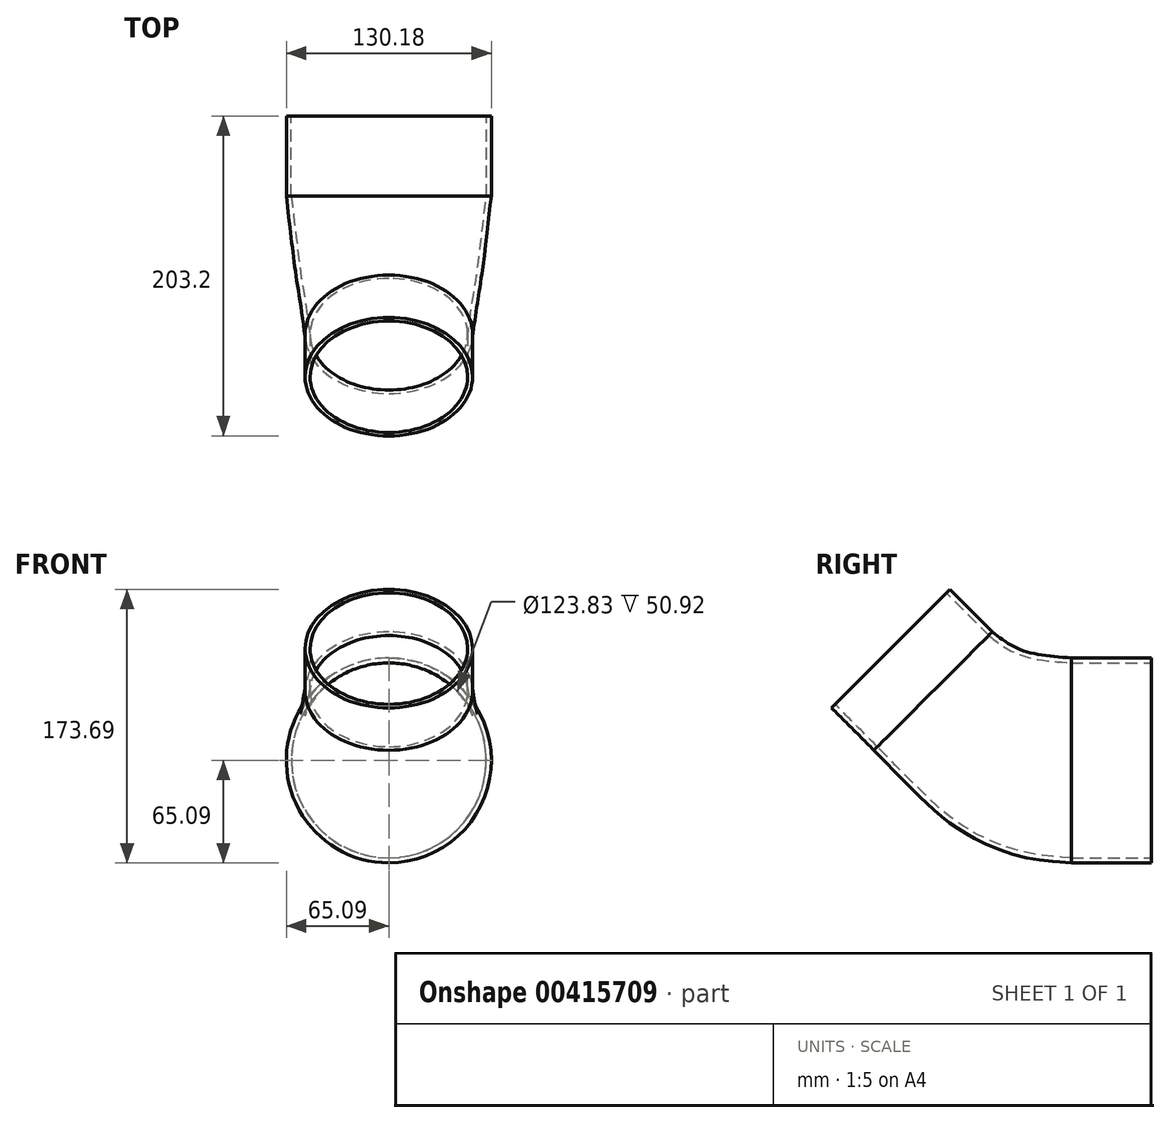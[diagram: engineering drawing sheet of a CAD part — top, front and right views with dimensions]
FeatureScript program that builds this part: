
annotation { "Feature Type Name" : "Feature", "Feature Type Description" : "" }
export const myFeature = defineFeature(function(context is Context, id is Id, definition is map)
    precondition{}
    {
        {
            var Q0;
            Q0=qCreatedBy(makeId("Front.planeOp"),FACE);
            var sketch = newSketch(context, id + "F0", { "sketchPlane" : qUnion([Q0])});
            skCircle(sketch, "E0", {"center": v(0, 0) * mm, "radius": 65.09 * mm});
            skSolve(sketch);
        }
        {
            var Q0;
            Q0=makeQuery(id+"F0.imprint","IMPRINT",FACE,{"disambiguationData":[TD([[makeQuery(id+"F0.imprint","IMPRINT",EDGE,{"derivedFrom":sQuery(id+"F0.wireOp",EDGE,"E0")}),1.0]])]});
            extrude(context, id + "F1", {"entities" : qUnion([Q0]), "depth" : 50.8 * mm});
        }
        {
            var Q0;
            Q0=qCreatedBy(makeId("Right.planeOp"),FACE);
            var sketch = newSketch(context, id + "F2", { "sketchPlane" : qUnion([Q0])});
            skLineSegment(sketch, "E1", {"start": v(0, -65.09) * mm, "end": v(-50.8, -65.09) * mm});
            skLineSegment(sketch, "E2", {"start": v(-50.8, 65.09) * mm, "end": v(0, 65.09) * mm});
            skLineSegment(sketch, "E3", {"start": v(-50.8, 65.09) * mm, "end": v(-142.85, -26.96) * mm, "construction": true});
            skLineSegment(sketch, "E4", {"start": v(0, 65.09) * mm, "end": v(-203.2, 65.09) * mm, "construction": true});
            skLineSegment(sketch, "E5", {"start": v(-142.85, -26.96) * mm, "end": v(-203.2, 33.4) * mm});
            skLineSegment(sketch, "E6", {"start": v(-203.2, 65.09) * mm, "end": v(-203.2, 33.4) * mm, "construction": true});
            skLineSegment(sketch, "E7", {"start": v(-203.2, 33.4) * mm, "end": v(-110.4, 126.2) * mm, "construction": true});
            skArc(sketch, "E8.trimOffspring", {"start": v(-142.85, -26.96) * mm, "mid": v(-100.62, -55.18) * mm, "end": v(-50.8, -65.09) * mm});
            skArc(sketch, "E9", {"start": v(-96.82, 19.06) * mm, "mid": v(-75.7, 4.95) * mm, "end": v(-50.8, 0) * mm});
            skLineSegment(sketch, "E10.0", {"start": v(-50.8, -65.09) * mm, "end": v(-50.8, 65.09) * mm});
            skSolve(sketch);
        }
        {
            var Q0;
            Q0=sQuery(id+"F2.wireOp",EDGE,"E7");
            cPlane(context, id + "F3", {"entities" : qUnion([Q0]), "cplaneType" : CPlaneType.LINE_ANGLE, "offset" : 25.4 * mm, "angle" : 0 * degree, "width" : 152.4 * mm, "height" : 152.4 * mm});
        }
        {
            var Q0;
            Q0=qCreatedBy(id+"F3.planeOp",FACE);
            var sketch = newSketch(context, id + "F4", { "sketchPlane" : qUnion([Q0])});
            skLineSegment(sketch, "E11.0", {"start": v(0, -120.07) * mm, "end": v(0, 11.18) * mm, "construction": true});
            skCircle(sketch, "E12", {"center": v(0, -66.9) * mm, "radius": 53.18 * mm});
            skSolve(sketch);
        }
        {
            var Q0;
            Q0=makeQuery(id+"F4.imprint","IMPRINT",FACE,{"disambiguationData":[TD([[makeQuery(id+"F4.imprint","IMPRINT",EDGE,{"derivedFrom":sQuery(id+"F4.wireOp",EDGE,"E12")}),1.0]])]});
            var Q1;
            Q1=sQuery(id+"F4.wireOp",EDGE,"E11.0");
            var Q2;
            Q2=sQuery(id+"F4.wireOp",EDGE,"E12");
            extrude(context, id + "F5", {"entities" : qUnion([Q0]), "operationType" : NewBodyOperationType.ADD, "surfaceEntities" : qUnion([Q1, Q2]), "oppositeDirection" : true, "depth" : 38.1 * mm});
        }
        {
            var Q0;
            Q0=qCreatedBy(makeId("Right.planeOp"),FACE);
            var sketch = newSketch(context, id + "F6", { "sketchPlane" : qUnion([Q0])});
            skPoint(sketch, "E13.0", {"position": v(-50.8, 65.09) * mm});
            skPoint(sketch, "E14.0", {"position": v(-50.8, -65.09) * mm});
            skLineSegment(sketch, "E15.0", {"start": v(-50.8, 65.09) * mm, "end": v(-142.85, -26.96) * mm, "construction": true});
            skLineSegment(sketch, "E16", {"start": v(-128, 108.6) * mm, "end": v(-101.05, 81.66) * mm, "construction": true});
            skFitSpline(sketch, "E17", {"points": [v(-50.8, 65.09) * mm, v(-82.75, 70.17) * mm, v(-101.05, 81.66) * mm], "startDerivative": vector(-62.84, 4.75) * mm, "endDerivative": vector(-36.78, 29.22) * mm});
            skLineSegment(sketch, "E18.0", {"start": v(-142.85, -26.96) * mm, "end": v(-176.26, 6.45) * mm});
            skArc(sketch, "E19.0", {"start": v(-142.85, -26.96) * mm, "mid": v(-100.62, -55.18) * mm, "end": v(-50.8, -65.09) * mm});
            skPoint(sketch, "E20.orphan", {"position": v(-203.2, 33.4) * mm});
            skFitSpline(sketch, "E21", {"points": [v(-50.8, -65.09) * mm, v(-85.52, -60.37) * mm, v(-117.86, -46.48) * mm, v(-139.58, -30.11) * mm, v(-176.26, 6.45) * mm], "startDerivative": vector(-142.28, 10.17) * mm, "endDerivative": vector(-133.17, 136.5) * mm});
            skSolve(sketch);
        }
        {
            var Q0;
            Q0=makeQuery(id+"F1.opExtrude","CAP_FACE",FACE,{"disambiguationData":[OSD([sQuery(id+"F0.wireOp",EDGE,"E0")])],"isStart":false});
            var Q1;
            Q1=makeQuery(id+"F5.opExtrude","CAP_FACE",FACE,{"disambiguationData":[OSD([sQuery(id+"F4.wireOp",EDGE,"E12")])],"isStart":false});
            var Q2;
            Q2=sQuery(id+"F6.wireOp",EDGE,"E17");
            var Q3;
            Q3=sQuery(id+"F6.wireOp",EDGE,"E21");
            loft(context, id + "F7", {"operationType" : NewBodyOperationType.ADD, "addGuides" : true, "sheetProfilesArray" : [{ "sheetProfileEntities" : qUnion([Q0]) }, { "sheetProfileEntities" : qUnion([Q1]) }], "guidesArray" : [{ "guideEntities" : qUnion([Q2]), "guideDerivativeType" : LoftGuideDerivativeType.DEFAULT, "guideDerivativeMagnitude" : 1 }, { "guideEntities" : qUnion([Q3]), "guideDerivativeType" : LoftGuideDerivativeType.DEFAULT, "guideDerivativeMagnitude" : 1 }]});
        }
        {
            var Q0;
            Q0=makeQuery(id+"F1.opExtrude","CAP_FACE",FACE,{"disambiguationData":[OSD([sQuery(id+"F0.wireOp",EDGE,"E0")])],"isStart":true});
            shell(context, id + "F8", {"entities" : qUnion([Q0]), "thickness" : 3.17 * mm});
        }
        {
            var Q0;
            Q0=makeQuery(id+"F5.opExtrude","CAP_FACE",FACE,{"disambiguationData":[OSD([sQuery(id+"F4.wireOp",EDGE,"E12")])],"isStart":true});
            var sketch = newSketch(context, id + "F9", { "sketchPlane" : qUnion([Q0])});
            skCircle(sketch, "E22", {"center": v(0, -66.9) * mm, "radius": 50 * mm});
            skSolve(sketch);
        }
        {
            var Q0;
            Q0 = qSketchRegion(id + "F9", true);
            extrude(context, id + "F10", {"entities" : qUnion([Q0]), "operationType" : NewBodyOperationType.REMOVE, "oppositeDirection" : true, "depth" : 3.17 * mm});
        }
    });
